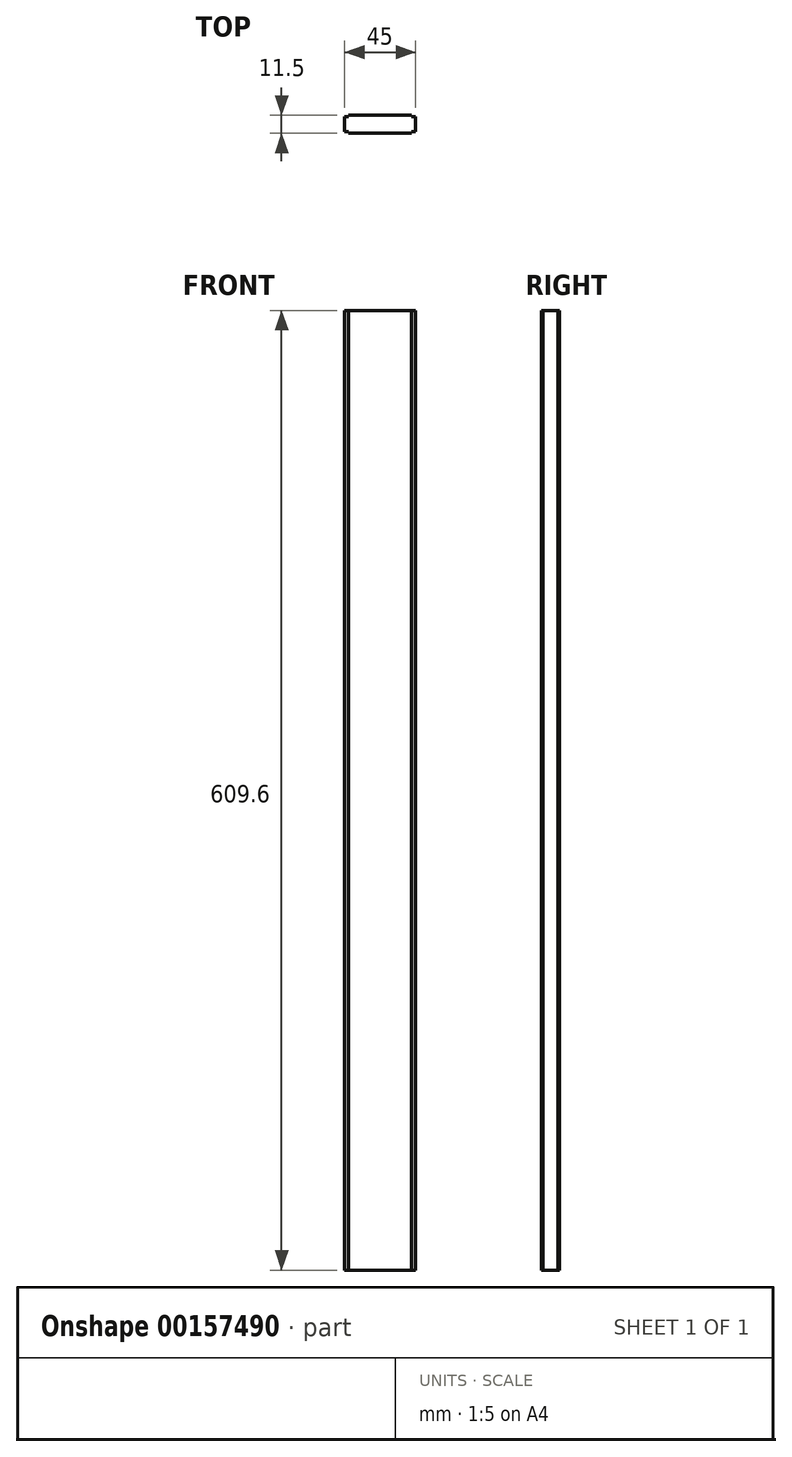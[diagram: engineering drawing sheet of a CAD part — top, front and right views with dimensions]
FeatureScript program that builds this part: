
annotation { "Feature Type Name" : "Feature", "Feature Type Description" : "" }
export const myFeature = defineFeature(function(context is Context, id is Id, definition is map)
    precondition{}
    {
        {
            var Q0;
            Q0=qCreatedBy(makeId("Top.planeOp"),FACE);
            var sketch = newSketch(context, id + "F0", { "sketchPlane" : qUnion([Q0])});
            skLineSegment(sketch, "E0.bottom", {"start": v(-22.5, -4.75) * mm, "end": v(22.5, -4.75) * mm});
            skLineSegment(sketch, "E0.top", {"start": v(-22.5, 4.75) * mm, "end": v(22.5, 4.75) * mm});
            skLineSegment(sketch, "E0.left", {"start": v(-22.5, -4.75) * mm, "end": v(-22.5, 4.75) * mm});
            skLineSegment(sketch, "E0.right", {"start": v(22.5, -4.75) * mm, "end": v(22.5, 4.75) * mm});
            skPoint(sketch, "E0.middle", {"position": v(0, 0) * mm});
            skSolve(sketch);
        }
        {
            var Q0;
            Q0=qSketchRegion(id+"F0",true);
            extrude(context, id + "F1", {"entities" : qUnion([Q0]), "depth" : 609.6 * mm});
        }
        {
            var Q0;
            Q0=makeQuery(id+"F1.opExtrude","SWEPT_FACE",FACE,{"disambiguationData":[OSD([sQuery(id+"F0.wireOp",EDGE,"E0.bottom")])]});
            var sketch = newSketch(context, id + "F2", { "sketchPlane" : qUnion([Q0])});
            skLineSegment(sketch, "E1.bottom", {"start": v(-20, 0) * mm, "end": v(20, 0) * mm});
            skLineSegment(sketch, "E1.top", {"start": v(-20, 609.6) * mm, "end": v(20, 609.6) * mm});
            skLineSegment(sketch, "E1.left", {"start": v(-20, 0) * mm, "end": v(-20, 609.6) * mm});
            skLineSegment(sketch, "E1.right", {"start": v(20, 0) * mm, "end": v(20, 609.6) * mm});
            skPoint(sketch, "E1.middle", {"position": v(0, 304.8) * mm});
            skPoint(sketch, "E1.middle.positionSnap0", {"position": v(22.5, 304.8) * mm});
            skPoint(sketch, "E1.centerSnap0", {"position": v(22.5, 304.8) * mm});
            skSolve(sketch);
        }
        {
            var Q0;
            Q0=qSketchRegion(id+"F2",true);
            extrude(context, id + "F3", {"entities" : qUnion([Q0]), "depth" : 1 * mm});
        }
        {
            var Q0;
            Q0=makeQuery(id+"F3.opExtrude","SWEPT_BODY",BODY,{"disambiguationData":[OSD([sQuery(id+"F2.wireOp",EDGE,"E1.bottom"),sQuery(id+"F2.wireOp",EDGE,"E1.top"),sQuery(id+"F2.wireOp",EDGE,"E1.left"),sQuery(id+"F2.wireOp",EDGE,"E1.right")])]});
            var Q1;
            Q1=qCreatedBy(makeId("Front.planeOp"),FACE);
            mirror(context, id + "F4", {"operationType" : NewBodyOperationType.ADD, "entities" : qUnion([Q0]), "mirrorPlane" : qUnion([Q1])});
        }
    });
